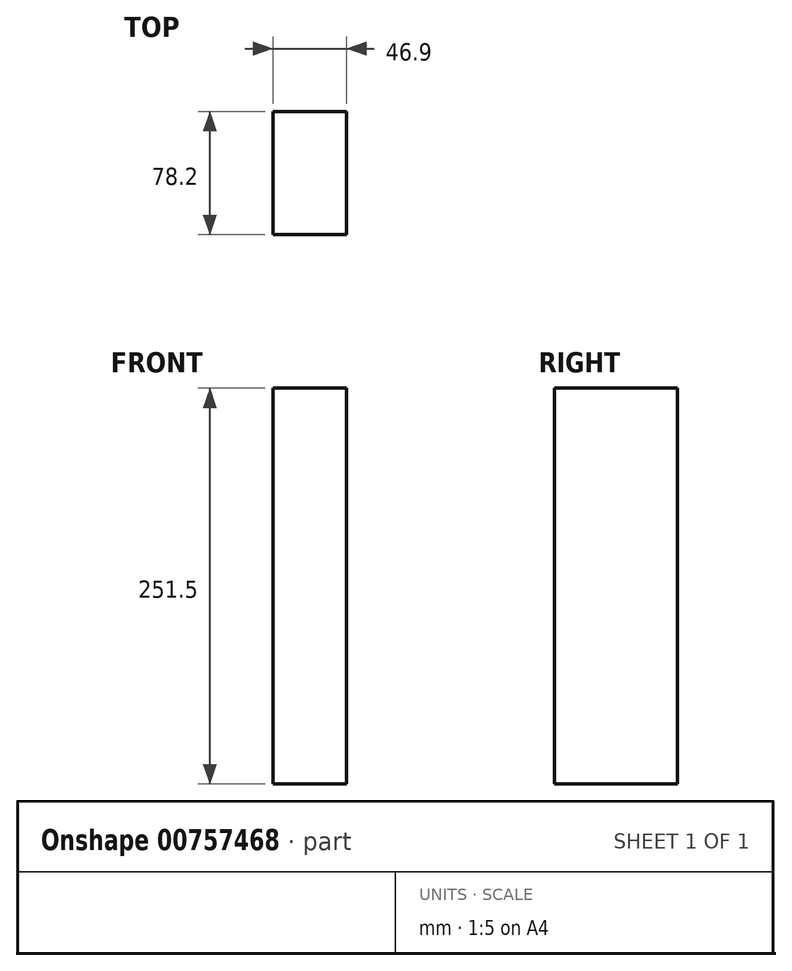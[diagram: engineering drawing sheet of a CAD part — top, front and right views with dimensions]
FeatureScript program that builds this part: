
annotation { "Feature Type Name" : "Feature", "Feature Type Description" : "" }
export const myFeature = defineFeature(function(context is Context, id is Id, definition is map)
    precondition{}
    {
        {
            var Q0;
            Q0=qCreatedBy(makeId("Right.planeOp"),FACE);
            var sketch = newSketch(context, id + "F0", { "sketchPlane" : qUnion([Q0])});
            skLineSegment(sketch, "E0.bottom", {"start": v(-39.1, 125.75) * mm, "end": v(39.1, 125.75) * mm});
            skLineSegment(sketch, "E0.top", {"start": v(-39.1, -125.75) * mm, "end": v(39.1, -125.75) * mm});
            skLineSegment(sketch, "E0.left", {"start": v(-39.1, 125.75) * mm, "end": v(-39.1, -125.75) * mm});
            skLineSegment(sketch, "E0.right", {"start": v(39.1, 125.75) * mm, "end": v(39.1, -125.75) * mm});
            skPoint(sketch, "E0.middle", {"position": v(0, 0) * mm});
            skSolve(sketch);
        }
        {
            var Q0;
            Q0 = qSketchRegion(id + "F0", true);
            extrude(context, id + "F1", {"entities" : qUnion([Q0]), "endBound" : BoundingType.SYMMETRIC, "oppositeDirection" : true, "depth" : 46.9 * mm, "offsetDistance" : 25 * mm});
        }
    });
